# Revit family: EZ_2
name_source: partatom
category: Lighting Fixtures
revit_build: Autodesk Revit 2014 (Build: 20130308_1515(x64)
units: mm (PartAtom-declared; Revit-internal decimal feet)

## types (1)
- EZ_2
    Apparent Load = 5 VA
    Application = The EZ-2 series is a commercial emergency lighting unit designed for fast
wall mount installation and reliable service. The EZ-2 has a flame-rated, UV
stable thermoplastic housing and a bright while textured finish. Lamp-heads
are fully adjustable. Unit provides a full 90 minutes of emergency lighting.
Includes fully automatic solid-state charger and lead calcium battery. The
EZ-2 accepts 120/277VAC input. Available with optional Spectron self-test/
self-diagnostic circuitry.
    Certification = UL 924 Listed
NFPA 101 Life Safety Code
CEC T20 Compliant
    Default Elevation = 48.000"
    Description = The Dual-Lite EZ-2 is a unique and efficient self-contained emergency lighting unit designed to meet a variety of needs.
    Electronics = Self-diagnostics monitors lamp status, lamp load transfer circuit and
battery capacity and displays any fault detection by means of a flashing code
• Self-Test feature automatically runs a peiodic emergency test to ensure
proper operation. Multi-color LED indicator provides visible fault detection
and charging status
• User initiated 1, 5, 30, or 60-minute system test feature
• 15 minute re-transfer delay
• Temperature compensated charger
• AC Lock-out circuit
• Automatic unit transfer in brown-out conditions(exceeding 20% of nominal)
    Finish = Hubbell - White
    Glass = Hubbell - light Glass
    Holder Material = Hubbell - Steel
    Lamp = LED Lamp
    Length = 16.563"
    Lens = Hubbell - Green Glass
    Load Classification = Lighting
    Manufacturer = DUAL-LITE
    Model = EZ-2 Series
    Operating Temperature Range = Standard Models: 688°F to 86°F (20° to 30°C), Damp Location Model: 32°F to 104°F (0° to 40°C)
    Product Documentation Link = https://hubbellcdn.com
    Product Page URL = https://www.hubbell.com
    Standard Features = • External push-to-test switch and AC-on indicator
• Battery re-charge per UL time limits
• Low voltage disconnect
• Conduit entry knock-out located at the top center
    Type Comments = Exit Light
    URL = https://www.hubbell.com
    Wall Plate Material = Hubbell - Steel
    Warranty = Standard Model- Full 3 year warranty
Spectron EZ-2I- Full 5 year warranty
    Wattage Comments = 5.4W
    Watts = 5 W

## geometry (parser evidence)
native form markers: Blend x8, Sweep x5
no freeform markers — native parametric forms only
